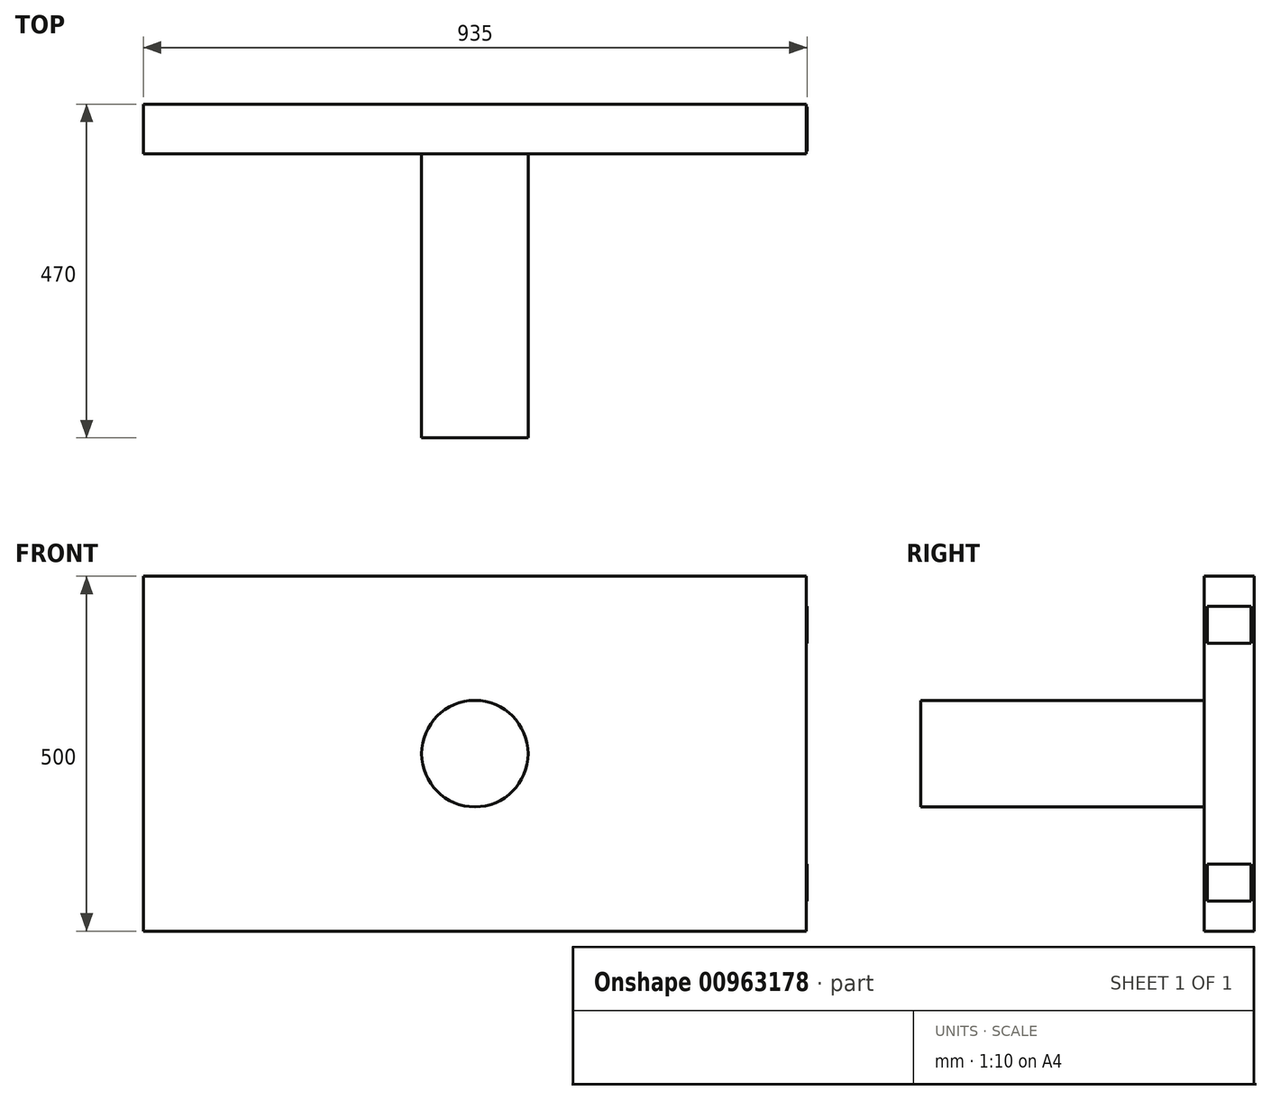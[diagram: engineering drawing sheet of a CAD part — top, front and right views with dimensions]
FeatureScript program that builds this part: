
annotation { "Feature Type Name" : "Feature", "Feature Type Description" : "" }
export const myFeature = defineFeature(function(context is Context, id is Id, definition is map)
    precondition{}
    {
        {
            var Q0;
            Q0=qCreatedBy(makeId("Front.planeOp"),FACE);
            var sketch = newSketch(context, id + "F0", { "sketchPlane" : qUnion([Q0])});
            skLineSegment(sketch, "E0.bottom", {"start": v(467, -250) * mm, "end": v(-467, -250) * mm});
            skLineSegment(sketch, "E0.top", {"start": v(467, 250) * mm, "end": v(-467, 250) * mm});
            skLineSegment(sketch, "E0.left", {"start": v(467, -250) * mm, "end": v(467, 250) * mm});
            skLineSegment(sketch, "E0.right", {"start": v(-467, -250) * mm, "end": v(-467, 250) * mm});
            skPoint(sketch, "E0.middle", {"position": v(0, 0) * mm});
            skSolve(sketch);
        }
        {
            var Q0;
            Q0=makeQuery(id+"F0.imprint","IMPRINT",FACE,{"disambiguationData":[TD([[makeQuery(id+"F0.imprint","IMPRINT",EDGE,{"derivedFrom":sQuery(id+"F0.wireOp",EDGE,"E0.bottom")}),-1.0]])]});
            extrude(context, id + "F1", {"entities" : qUnion([Q0]), "depth" : 70 * mm, "offsetDistance" : 25 * mm});
        }
        {
            var Q0;
            Q0=makeQuery(id+"F1.opExtrude","CAP_FACE",FACE,{"disambiguationData":[OSD([sQuery(id+"F0.wireOp",EDGE,"E0.bottom"),sQuery(id+"F0.wireOp",EDGE,"E0.top"),sQuery(id+"F0.wireOp",EDGE,"E0.left"),sQuery(id+"F0.wireOp",EDGE,"E0.right")])],"isStart":false});
            var sketch = newSketch(context, id + "F2", { "sketchPlane" : qUnion([Q0])});
            skCircle(sketch, "E1", {"center": v(0, 0) * mm, "radius": 75 * mm});
            skSolve(sketch);
        }
        {
            var Q0;
            Q0=makeQuery(id+"F2.imprint","IMPRINT",FACE,{"disambiguationData":[TD([[makeQuery(id+"F2.imprint","IMPRINT",EDGE,{"derivedFrom":sQuery(id+"F2.wireOp",EDGE,"E1")}),1.0]])]});
            extrude(context, id + "F3", {"entities" : qUnion([Q0]), "operationType" : NewBodyOperationType.ADD, "depth" : 400 * mm, "offsetDistance" : 25 * mm});
        }
        {
            var Q0;
            Q0=makeQuery(id+"F1.opExtrude","SWEPT_FACE",FACE,{"disambiguationData":[OSD([sQuery(id+"F0.wireOp",EDGE,"E0.left")])]});
            var sketch = newSketch(context, id + "F4", { "sketchPlane" : qUnion([Q0])});
            skLineSegment(sketch, "E2.bottom", {"start": v(-4, 155.6) * mm, "end": v(-66, 155.6) * mm});
            skLineSegment(sketch, "E2.top", {"start": v(-4, 207.4) * mm, "end": v(-66, 207.4) * mm});
            skLineSegment(sketch, "E2.left", {"start": v(-4, 155.6) * mm, "end": v(-4, 207.4) * mm});
            skLineSegment(sketch, "E2.right", {"start": v(-66, 155.6) * mm, "end": v(-66, 207.4) * mm});
            skPoint(sketch, "E2.middle", {"position": v(-35, 181.5) * mm});
            skLineSegment(sketch, "E3", {"start": v(-35, -261.1) * mm, "end": v(-35, 260.54) * mm, "construction": true});
            skPoint(sketch, "E3.startSnap0", {"position": v(-35, 250) * mm});
            skLineSegment(sketch, "E4.MirrorCS", {"start": v(-4, -155.6) * mm, "end": v(-66, -155.6) * mm});
            skLineSegment(sketch, "E5.MirrorCS", {"start": v(-4, -207.4) * mm, "end": v(-66, -207.4) * mm});
            skPoint(sketch, "E6.MirrorP", {"position": v(-35, -181.5) * mm});
            skLineSegment(sketch, "E7.MirrorCS", {"start": v(-4, -155.6) * mm, "end": v(-4, -207.4) * mm});
            skLineSegment(sketch, "E8.MirrorCS", {"start": v(-66, -155.6) * mm, "end": v(-66, -207.4) * mm});
            skSolve(sketch);
        }
        {
            var Q0;
            Q0=makeQuery(id+"F4.imprint","IMPRINT",FACE,{"disambiguationData":[TD([[makeQuery(id+"F4.imprint","IMPRINT",EDGE,{"derivedFrom":sQuery(id+"F4.wireOp",EDGE,"E2.bottom")}),-1.0]])]});
            var Q1;
            Q1=makeQuery(id+"F4.imprint","IMPRINT",FACE,{"disambiguationData":[TD([[makeQuery(id+"F4.imprint","IMPRINT",EDGE,{"derivedFrom":sQuery(id+"F4.wireOp",EDGE,"E4.MirrorCS")}),1.0]])]});
            extrude(context, id + "F5", {"entities" : qUnion([Q0, Q1]), "operationType" : NewBodyOperationType.ADD, "depth" : 1 * mm, "offsetDistance" : 25 * mm});
        }
        {
            var Q0;
            Q0=qCreatedBy(makeId("Right.planeOp"),FACE);
            cPlane(context, id + "F6", {"entities" : qUnion([Q0]), "cplaneType" : CPlaneType.OFFSET, "offset" : 0 * mm, "width" : 150 * mm, "height" : 150 * mm});
        }
    });
